# Revit family: Electronics_Loudspeaker_Bose-Professional_Designmax_DM3SE
name_source: partatom
category: Communication Devices
revit_build: Autodesk Revit 2017 (Build: 20190508_0315(x64)
units: mm (PartAtom-declared; Revit-internal decimal feet)

## family parameters
Cut with Voids When Loaded = No
Host = Face
Maintain Annotation Orientation = No
OmniClass Number = 23.85.10.11.14.14.14
OmniClass Title = Loudspeakers
Part Type = Normal
Room Calculation Point = No
Round Connector Dimension = Use Diameter
Shared = No

## types (2) — shared parameters
Assembly Code = D5030
Bracket Material = Metal-Bose-Aluminium
Crossover = 1.7 kHz (passive 2-way crossover)
Default Elevation = 1219 mm
Depth = 154 mm
Description = Premium sound to maximize any design.
DesignMax loudspeakers bring outstanding audio and aesthetics to any commercial space. With 12 models to choose from, it’s easy to create tailored solutions that deliver instantly impressive sound. QuickHold mounting mechanisms make installation efficient, reducing strain and hassle — and saving substantial time. And with both black and white versions available, DesignMax loudspeakers integrate seamlessly with any décor.

The 25-watt DesignMax DM3SE loudspeaker features a two-way 3.5-inch woofer and ¾-inch tweeter coaxially mounted within the Dispersion Alignment system, producing a frequency range of 70 Hz - 20 kHz. The DM3SE is surface-mounted, IP55 outdoor-rated, and locks onto a hidden QuickHold U-bracket for fast, secure installation. 

FEATURES
Combine models to complete any design, big or small — 12 loudspeakers to mix and match, from 2-inch, low-profile models to 8-inch, high-SPL compression-driver loudspeakers and outdoor-rated options

Deliver instantly impressive sound with custom Bose drivers — no DSP or EQ required. For even better sound, use select Bose DSPs and amplifiers to enable Bose loudspeaker EQ and SmartBass processing, which expands performance and response at any listening level

Ensure a consistent listening experience throughout the room with the Dispersion Alignment system, which matches the coverage of the woofer to the pattern of the tweeter

Blend into any room design with elegant form factors, minimum-bezel grilles available in black or white, and removable logos

Reduce installation time with the patented QuickHold mounting system, which also reduces strain, hassle, and the chance of product damage

Install easily — all models include Euroblock connectors; ceiling-mounted models include plenum-rated backcans, tile-bridges, and front-access audio wiring that makes installation and troubleshooting easier

Install DM3SE outside — IP55 rating with standard aluminum grille for outdoor use 

Applications
Performing arts venues
Places of worship
Conference centers
Retail stores
Restaurants and bars
Hospitality venues
Edition number = 1
Environmental = Outdoor per IEC 529 IP55 (suitable for use outdoors in wet locations), includes aluminum grille to prevent red corrosion and weather resistant input cover
Frequency Range = 70-20,000 Hz
Frequency Response = 85 – 20,000 Hz
HF Driver = 1 × 20 mm (0.75 in) neodymium dome tweeter, coaxially mounted, weather-treated
Height = 232 mm
Keynote = 16700
LF Driver = 1 × 83 mm woofer (3.25 in), weather-treated
Manufacturer = Bose Professional
Model = DesignMax DM3SE
Mounting/Suspension = QuickHold Mounting System with included U-Bracket 4 preset mounting angles: 0°, 15°, 30°, 45° for wall or ceiling placement Two (2) rear M6 screw inserts for use with optional pan & tilt bracket and one (1) rear M6 screw insert for safety-tether attachment
Nominal Coverage Pattern = 135° × 135°
Nominal Impedance = 8 Ω (transformer bypass)
Nominal Sensitivity = 84 dB
Operating Temperature Range = -25 °C to 70 °C (-13 °F to 158 °F)
Power Connector = Euroblock 6-pin connector with loop-through, mounted on rear. Accepts 18 AWG (0.8 mm2) to 14 AWG (2.5 mm2) size wire
Power Handling(Long-term continuous) = 25 W
Power Handling(peak) = 100 W
Product Guid = 2406d58d-87f1-41f2-a7b8-36c01991bd97
Product data url = https://www.bimobject.com
Rated Maximum SPL = 98 dB
Recommended High-pass Filter = 80 Hz with recommended 24 dB / octave filter
Transformer Taps Information = 70V: 3, 6, 12, 25 W, bypass  100V: 6, 12, 25 W, bypass
URL = https://www.bose.com
Weight = 2.80 kg
Width = 154 mm
Wire/ Conduit Entry = Accepts 18 AWG (0.8 mm2) to 14 AWG (2.5 mm2) size wire

## per-type parameters (varying)
| type | Mesh Material | Product code | Speaker Material |
| DM3SE-Black | Grill-Bose-Black | 829712-0110 | Metal-Bose-Black |
| DM3SE-White | Grill-Bose-White | 829712-0210 | Metal-Bose-White |

## geometry (parser evidence)
native form markers: Blend x8, Sweep x9
no freeform markers — native parametric forms only
